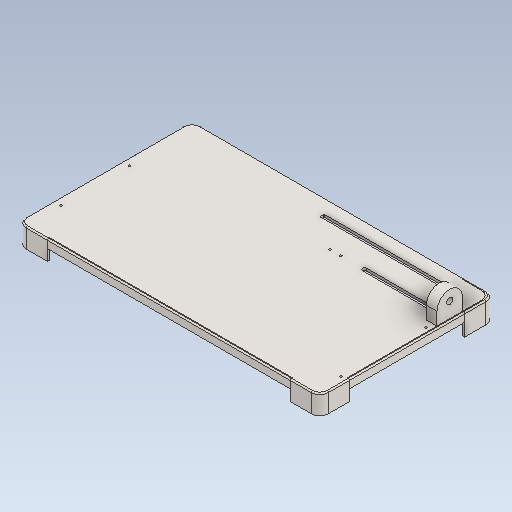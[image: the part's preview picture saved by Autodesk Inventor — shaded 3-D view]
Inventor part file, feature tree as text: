
AUTODESK INVENTOR PART (.ipt)
format: ipt  version: 2021 (Build 250183000, 183)  size: 185,344 bytes
history: mixed  units: mm
features: other x7, fillet x3, imported_body x1
ambient origin geometry x8: Origin, YZ Plane, XZ Plane, XY Plane, X Axis, Y Axis, Z Axis, Center Point
bodies: Body1 (imported_parasolid), Body2 (imported_parasolid), Body3 (imported_parasolid), Body4 (imported_parasolid), Body5 (imported_parasolid)
feature tree (11):
  other  "Sólido1"
  other  "Sólido2"
  other  "Sólido3"
  other  "Sólido4"
  other  "Sólido5"
  fillet  "Fillet3"  [1 undecoded]
  fillet  "Fillet4"  [1 undecoded]
  fillet  "Fillet6"  [1 undecoded]
  other  "Cut-Extrude3"
  other  "Ø5.0 (5) Diameter Hole3"
  imported_body  NMx_Import_Brep_tag  [imported B-rep: ~94 faces, bbox_mm=[710.0, 86.0, 410.0]]
note: 3 required parameter values undecoded (feature->parameter linkage not recoverable at this tier; creation-order binding heuristic only, values carry confidence <= 0.55)
